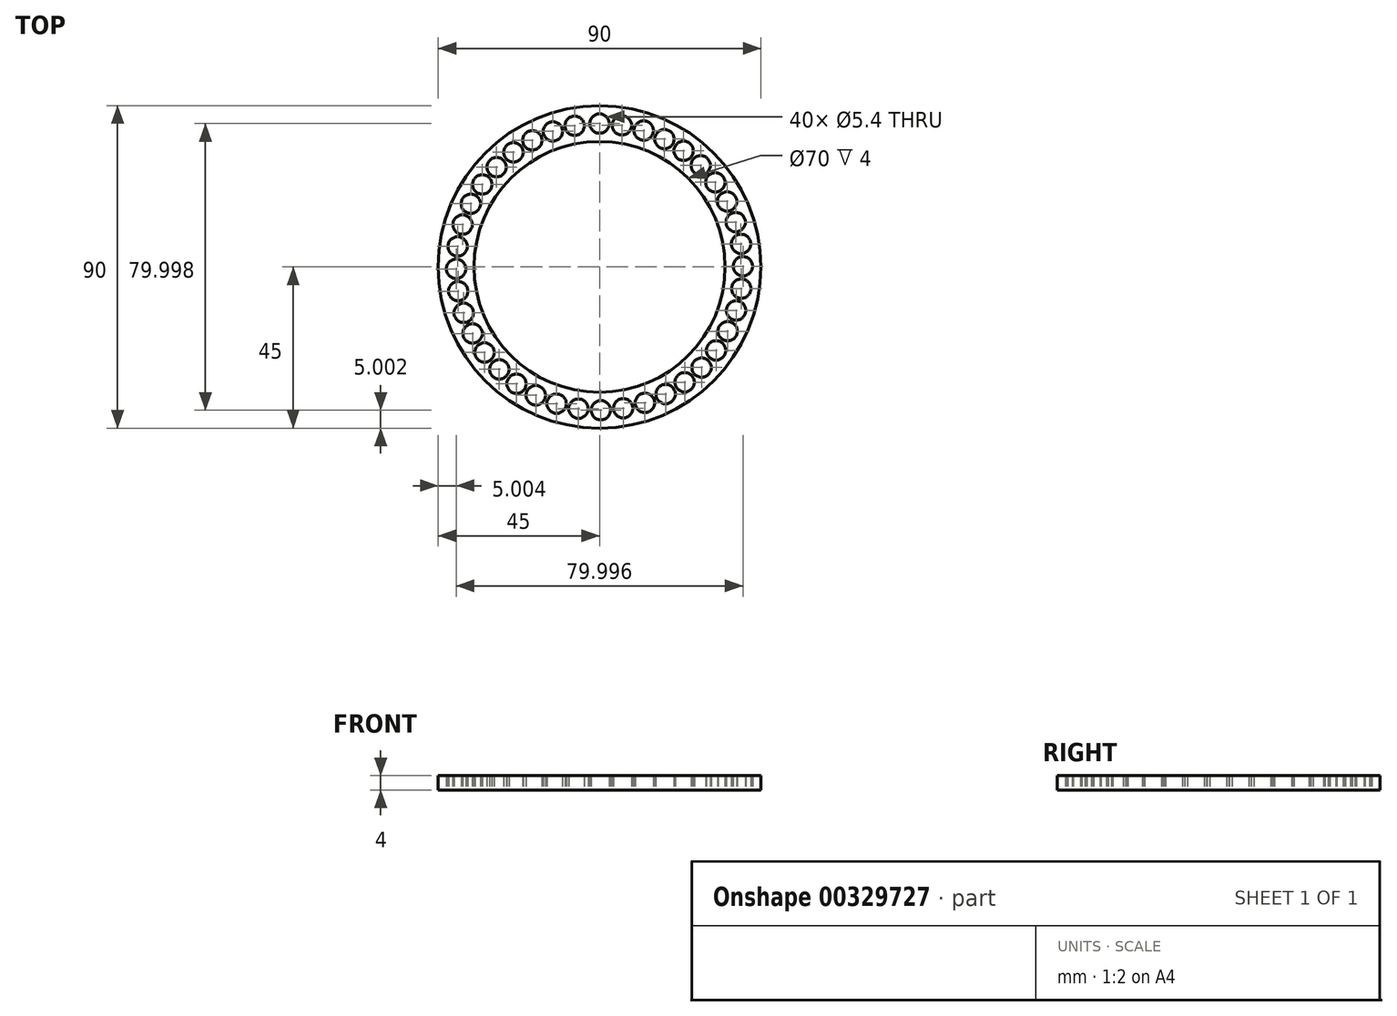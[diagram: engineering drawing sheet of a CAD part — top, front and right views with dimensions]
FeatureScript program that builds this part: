
annotation { "Feature Type Name" : "Feature", "Feature Type Description" : "" }
export const myFeature = defineFeature(function(context is Context, id is Id, definition is map)
    precondition{}
    {
        {
            var Q0;
            Q0=qCreatedBy(makeId("Top.planeOp"),FACE);
            var sketch = newSketch(context, id + "F0", { "sketchPlane" : qUnion([Q0])});
            skCircle(sketch, "E0", {"center": v(0, 0) * mm, "radius": 35 * mm});
            skCircle(sketch, "E1", {"center": v(0, 0) * mm, "radius": 45 * mm});
            skLineSegment(sketch, "E2", {"start": v(0, 0) * mm, "end": v(0, 40) * mm});
            skCircle(sketch, "E3", {"center": v(0, 40) * mm, "radius": 2.7 * mm});
            skCircle(sketch, "E4.1.0", {"center": v(6.24, 39.51) * mm, "radius": 2.7 * mm});
            skCircle(sketch, "E4.2.0", {"center": v(12.33, 38.05) * mm, "radius": 2.7 * mm});
            skCircle(sketch, "E4.3.0", {"center": v(18.11, 35.66) * mm, "radius": 2.7 * mm});
            skCircle(sketch, "E4.4.0", {"center": v(23.45, 32.4) * mm, "radius": 2.7 * mm});
            skCircle(sketch, "E4.5.0", {"center": v(28.22, 28.35) * mm, "radius": 2.7 * mm});
            skCircle(sketch, "E4.6.0", {"center": v(32.3, 23.6) * mm, "radius": 2.7 * mm});
            skCircle(sketch, "E4.7.0", {"center": v(35.58, 18.27) * mm, "radius": 2.7 * mm});
            skCircle(sketch, "E4.8.0", {"center": v(38, 12.5) * mm, "radius": 2.7 * mm});
            skCircle(sketch, "E4.9.0", {"center": v(39.48, 6.42) * mm, "radius": 2.7 * mm});
            skCircle(sketch, "E4.10.0", {"center": v(40, 0.18) * mm, "radius": 2.7 * mm});
            skCircle(sketch, "E4.11.0", {"center": v(39.54, -6.06) * mm, "radius": 2.7 * mm});
            skCircle(sketch, "E4.12.0", {"center": v(38.1, -12.16) * mm, "radius": 2.7 * mm});
            skCircle(sketch, "E4.13.0", {"center": v(35.75, -17.95) * mm, "radius": 2.7 * mm});
            skCircle(sketch, "E4.14.0", {"center": v(32.5, -23.3) * mm, "radius": 2.7 * mm});
            skCircle(sketch, "E4.15.0", {"center": v(28.47, -28.1) * mm, "radius": 2.7 * mm});
            skCircle(sketch, "E4.16.0", {"center": v(23.74, -32.2) * mm, "radius": 2.7 * mm});
            skCircle(sketch, "E4.17.0", {"center": v(18.43, -35.5) * mm, "radius": 2.7 * mm});
            skCircle(sketch, "E4.18.0", {"center": v(12.67, -37.94) * mm, "radius": 2.7 * mm});
            skCircle(sketch, "E4.19.0", {"center": v(6.6, -39.45) * mm, "radius": 2.7 * mm});
            skCircle(sketch, "E4.20.0", {"center": v(0.36, -40) * mm, "radius": 2.7 * mm});
            skCircle(sketch, "E4.21.0", {"center": v(-5.89, -39.56) * mm, "radius": 2.7 * mm});
            skCircle(sketch, "E4.22.0", {"center": v(-11.99, -38.16) * mm, "radius": 2.7 * mm});
            skCircle(sketch, "E4.23.0", {"center": v(-17.8, -35.83) * mm, "radius": 2.7 * mm});
            skCircle(sketch, "E4.24.0", {"center": v(-23.16, -32.61) * mm, "radius": 2.7 * mm});
            skCircle(sketch, "E4.25.0", {"center": v(-27.97, -28.6) * mm, "radius": 2.7 * mm});
            skCircle(sketch, "E4.26.0", {"center": v(-32.08, -23.89) * mm, "radius": 2.7 * mm});
            skCircle(sketch, "E4.27.0", {"center": v(-35.42, -18.59) * mm, "radius": 2.7 * mm});
            skCircle(sketch, "E4.28.0", {"center": v(-37.88, -12.84) * mm, "radius": 2.7 * mm});
            skCircle(sketch, "E4.29.0", {"center": v(-39.42, -6.77) * mm, "radius": 2.7 * mm});
            skCircle(sketch, "E4.30.0", {"center": v(-40, -0.54) * mm, "radius": 2.7 * mm});
            skCircle(sketch, "E4.31.0", {"center": v(-39.6, 5.7) * mm, "radius": 2.7 * mm});
            skCircle(sketch, "E4.32.0", {"center": v(-38.22, 11.81) * mm, "radius": 2.7 * mm});
            skCircle(sketch, "E4.33.0", {"center": v(-35.9, 17.63) * mm, "radius": 2.7 * mm});
            skCircle(sketch, "E4.34.0", {"center": v(-32.71, 23.02) * mm, "radius": 2.7 * mm});
            skCircle(sketch, "E4.35.0", {"center": v(-28.72, 27.84) * mm, "radius": 2.7 * mm});
            skCircle(sketch, "E4.36.0", {"center": v(-24.03, 31.98) * mm, "radius": 2.7 * mm});
            skCircle(sketch, "E4.37.0", {"center": v(-18.75, 35.33) * mm, "radius": 2.7 * mm});
            skCircle(sketch, "E4.38.0", {"center": v(-13, 37.83) * mm, "radius": 2.7 * mm});
            skCircle(sketch, "E4.39.0", {"center": v(-6.95, 39.4) * mm, "radius": 2.7 * mm});
            skLineSegment(sketch, "E4.anchor1", {"start": v(0, 0) * mm, "end": v(0, 40) * mm, "construction": true});
            skLineSegment(sketch, "E4.anchor2", {"start": v(0, 0) * mm, "end": v(-6.95, 39.4) * mm, "construction": true});
            skSolve(sketch);
        }
        {
            var Q0;
            Q0=makeQuery(id+"F0.imprint","IMPRINT",FACE,{"disambiguationData":[TD([[makeQuery(id+"F0.imprint","IMPRINT",EDGE,{"derivedFrom":sQuery(id+"F0.wireOp",EDGE,"E0")}),-1.0]])]});
            extrude(context, id + "F1", {"entities" : qUnion([Q0]), "endBound" : BoundingType.SYMMETRIC, "depth" : 4 * mm});
        }
    });
